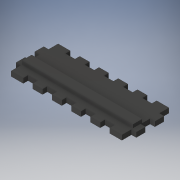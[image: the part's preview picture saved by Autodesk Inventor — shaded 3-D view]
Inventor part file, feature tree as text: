
AUTODESK INVENTOR PART (.ipt)
format: ipt  version: 2019 (Build 230136000, 136)  size: 207,872 bytes
history: native  units: mm
features: extrude x3, sketch x3, projected_geometry x1
ambient origin geometry x8: Origin, YZ Plane, XZ Plane, XY Plane, X Axis, Y Axis, Z Axis, Center Point
bodies: Solid1 (feature_tree)
feature tree (7):
  extrude  "Extrusion1"  Depth=39.0mm
  extrude  "Extrusion2"  Depth=4.0mm
  extrude  "Extrusion3"  Depth=8.0mm
  sketch  "Sketch1"  dims[d0=100.0mm d1=39.0mm]
  sketch  "Sketch2"  dims[d2=4.0mm d3=0.0mm d4=4.0mm]
  projected_geometry  "Projected Loop1"
  sketch  "Sketch3"  dims[d5=4.0mm d7=8.0mm d8=8.0mm d10=8.0mm d11=8.0mm d13=4.0mm d14=8.0mm d15=4.0mm d16=0.0mm d17=5.0mm d18=8.0mm d19=3.0mm d20=0.0mm]
